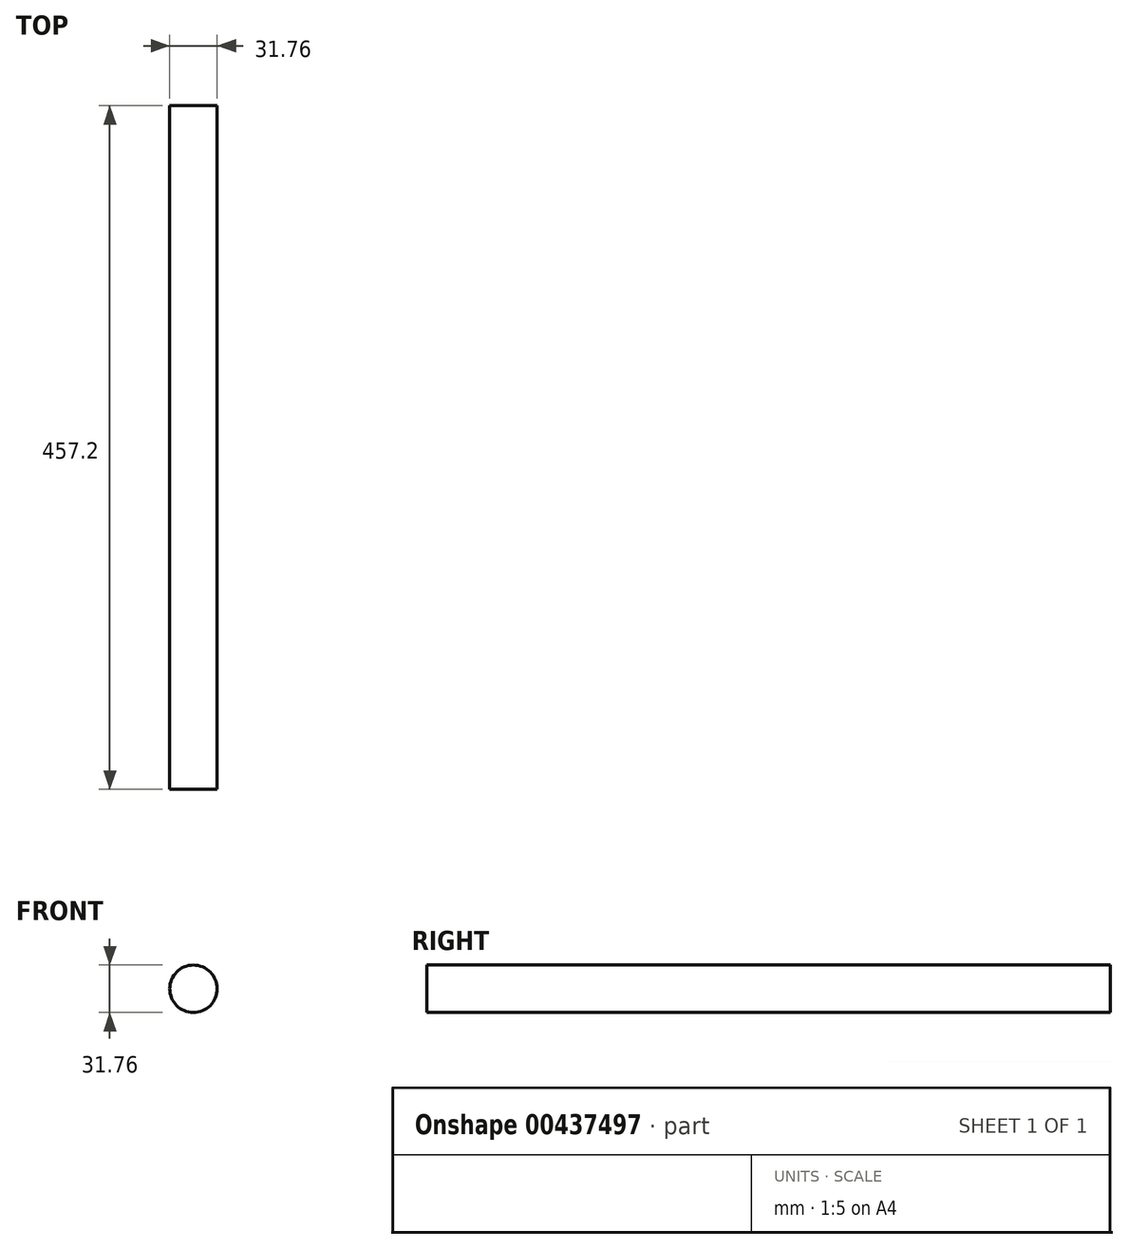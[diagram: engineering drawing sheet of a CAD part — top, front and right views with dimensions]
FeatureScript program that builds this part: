
annotation { "Feature Type Name" : "Feature", "Feature Type Description" : "" }
export const myFeature = defineFeature(function(context is Context, id is Id, definition is map)
    precondition{}
    {
        {
            var Q0;
            Q0=qCreatedBy(makeId("Front.planeOp"),FACE);
            var sketch = newSketch(context, id + "F0", { "sketchPlane" : qUnion([Q0])});
            skCircle(sketch, "E0", {"center": v(0, 0) * mm, "radius": 15.88 * mm});
            skSolve(sketch);
        }
        {
            var Q0;
            Q0=makeQuery(id+"F0.imprint","IMPRINT",FACE,{"disambiguationData":[TD([[makeQuery(id+"F0.imprint","IMPRINT",EDGE,{"derivedFrom":sQuery(id+"F0.wireOp",EDGE,"E0")}),1.0]])]});
            extrude(context, id + "F1", {"entities" : qUnion([Q0]), "depth" : 457.2 * mm, "offsetDistance" : 25.4 * mm});
        }
    });
